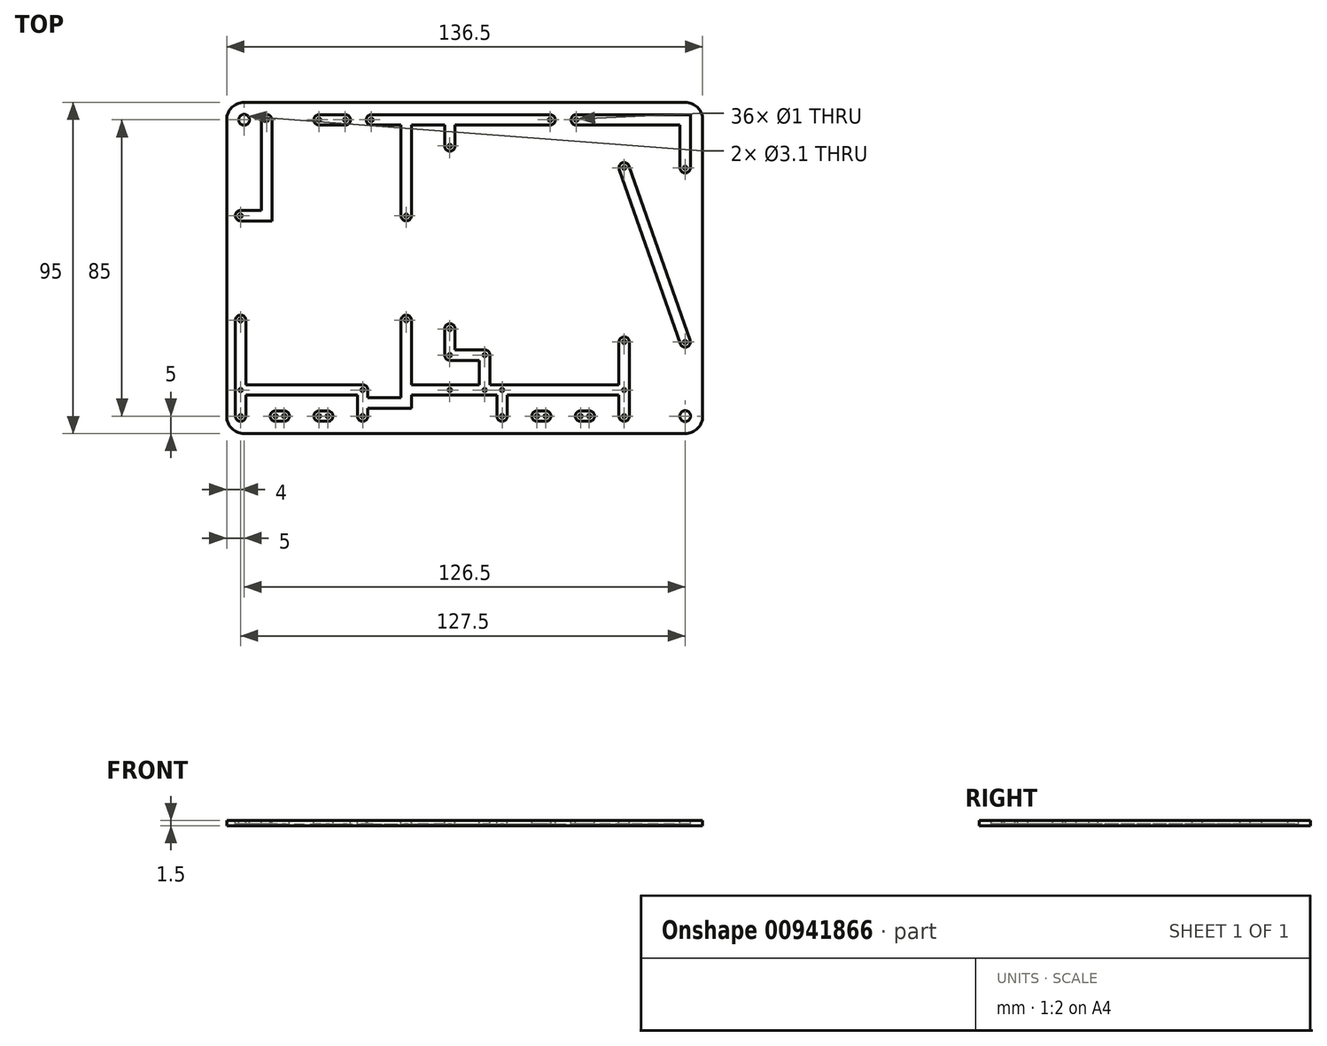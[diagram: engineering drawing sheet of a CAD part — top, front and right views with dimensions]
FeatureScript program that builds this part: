
annotation { "Feature Type Name" : "Feature", "Feature Type Description" : "" }
export const myFeature = defineFeature(function(context is Context, id is Id, definition is map)
    precondition{}
    {
        {
            var Q0;
            Q0=qCreatedBy(makeId("Top.planeOp"),FACE);
            var sketch = newSketch(context, id + "F0", { "sketchPlane" : qUnion([Q0])});
            skLineSegment(sketch, "E0", {"start": v(5, 60) * mm, "end": v(5, 7.5) * mm, "construction": true});
            skLineSegment(sketch, "E1", {"start": v(5, 0) * mm, "end": v(5, -10) * mm, "construction": true});
            skLineSegment(sketch, "E2", {"start": v(33.75, 67.5) * mm, "end": v(41.25, 67.5) * mm, "construction": true});
            skPoint(sketch, "E3", {"position": v(33.75, 67.5) * mm});
            skPoint(sketch, "E4.orphan", {"position": v(5, 67.5) * mm});
            skLineSegment(sketch, "E5", {"start": v(15, 0) * mm, "end": v(15, -10) * mm, "construction": true});
            skPoint(sketch, "E6", {"position": v(5, -17.5) * mm});
            skLineSegment(sketch, "E7", {"start": v(20, -17.5) * mm, "end": v(55, -17.5) * mm, "construction": true});
            skPoint(sketch, "E8", {"position": v(30, -17.5) * mm});
            skPoint(sketch, "E9", {"position": v(32.5, -17.5) * mm});
            skPoint(sketch, "E10", {"position": v(42.5, -17.5) * mm});
            skPoint(sketch, "E11", {"position": v(45, -17.5) * mm});
            skPoint(sketch, "E12", {"position": v(37.5, 67.5) * mm});
            skPoint(sketch, "E13", {"position": v(37.5, -17.5) * mm});
            skLineSegment(sketch, "E14", {"start": v(-7.5, 40) * mm, "end": v(-7.5, 10) * mm, "construction": true});
            skLineSegment(sketch, "E15", {"start": v(-7.5, 25) * mm, "end": v(0, 25) * mm, "construction": true});
            skPoint(sketch, "E16", {"position": v(-7.5, 40) * mm});
            skPoint(sketch, "E17.MirrorP", {"position": v(-7.5, 10) * mm});
            skPoint(sketch, "E18.orphan", {"position": v(-7.5, 67.5) * mm});
            skPoint(sketch, "E19.orphan", {"position": v(-7.5, -17.5) * mm});
            skLineSegment(sketch, "E20", {"start": v(-17.5, 67.5) * mm, "end": v(-25, 67.5) * mm, "construction": true});
            skLineSegment(sketch, "E21", {"start": v(-32.5, 67.5) * mm, "end": v(-47.5, 67.5) * mm, "construction": true});
            skLineSegment(sketch, "E22", {"start": v(-55, 40) * mm, "end": v(-55, 10) * mm, "construction": true});
            skPoint(sketch, "E23", {"position": v(-55, 40) * mm});
            skPoint(sketch, "E24", {"position": v(-55, 10) * mm});
            skPoint(sketch, "E25.orphan", {"position": v(-55, 67.5) * mm});
            skPoint(sketch, "E26.orphan", {"position": v(-55, -17.5) * mm});
            skPoint(sketch, "E27.MirrorP", {"position": v(-45, -17.5) * mm});
            skLineSegment(sketch, "E28.MirrorCS", {"start": v(-20, -17.5) * mm, "end": v(-55, -17.5) * mm, "construction": true});
            skPoint(sketch, "E29.MirrorP", {"position": v(-30, -17.5) * mm});
            skPoint(sketch, "E30.MirrorP", {"position": v(-37.5, -17.5) * mm});
            skPoint(sketch, "E31.MirrorP", {"position": v(-42.5, -17.5) * mm});
            skPoint(sketch, "E32.MirrorP", {"position": v(-32.5, -17.5) * mm});
            skLineSegment(sketch, "E33", {"start": v(-55, -10) * mm, "end": v(-20, -10) * mm, "construction": true});
            skLineSegment(sketch, "E34.MirrorCS", {"start": v(55, -10) * mm, "end": v(20, -10) * mm, "construction": true});
            skLineSegment(sketch, "E35", {"start": v(55, 53.75) * mm, "end": v(55, 3.75) * mm, "construction": true});
            skPoint(sketch, "E36", {"position": v(55, 28.75) * mm});
            skPoint(sketch, "E37", {"position": v(55, 53.75) * mm});
            skLineSegment(sketch, "E38", {"start": v(55, 28.75) * mm, "end": v(72.5, 28.75) * mm, "construction": true});
            skPoint(sketch, "E39.MirrorP", {"position": v(55, 3.75) * mm});
            skPoint(sketch, "E40.orphan", {"position": v(55, 67.5) * mm});
            skLineSegment(sketch, "E41", {"start": v(63.75, 28.75) * mm, "end": v(63.75, 53.75) * mm, "construction": true});
            skLineSegment(sketch, "E42.MirrorCS", {"start": v(72.5, 53.75) * mm, "end": v(72.5, 3.75) * mm, "construction": true});
            skLineSegment(sketch, "E43.bottom", {"start": v(77.5, -27.5) * mm, "end": v(-77.5, -27.5) * mm});
            skLineSegment(sketch, "E43.top", {"start": v(77.5, 85) * mm, "end": v(-77.5, 85) * mm});
            skLineSegment(sketch, "E43.left", {"start": v(82.5, -22.5) * mm, "end": v(82.5, 80) * mm});
            skLineSegment(sketch, "E43.right", {"start": v(-82.5, -22.5) * mm, "end": v(-82.5, 80) * mm});
            skPoint(sketch, "E43.middle", {"position": v(0, 28.75) * mm});
            skPoint(sketch, "E44.visualSharp", {"position": v(-82.5, 85) * mm});
            skArc(sketch, "E44.filletArc", {"start": v(-77.5, 85) * mm, "mid": v(-81.04, 83.54) * mm, "end": v(-82.5, 80) * mm});
            skPoint(sketch, "E45.visualSharp", {"position": v(82.5, 85) * mm});
            skArc(sketch, "E45.filletArc", {"start": v(82.5, 80) * mm, "mid": v(81.04, 83.54) * mm, "end": v(77.5, 85) * mm});
            skPoint(sketch, "E46.visualSharp", {"position": v(82.5, -27.5) * mm});
            skArc(sketch, "E46.filletArc", {"start": v(77.5, -27.5) * mm, "mid": v(81.04, -26.04) * mm, "end": v(82.5, -22.5) * mm});
            skPoint(sketch, "E47.visualSharp", {"position": v(-82.5, -27.5) * mm});
            skArc(sketch, "E47.filletArc", {"start": v(-82.5, -22.5) * mm, "mid": v(-81.04, -26.04) * mm, "end": v(-77.5, -27.5) * mm});
            skCircle(sketch, "E48", {"center": v(-55, 40) * mm, "radius": 0.5 * mm});
            skCircle(sketch, "E49", {"center": v(-55, 10) * mm, "radius": 0.5 * mm});
            skCircle(sketch, "E50", {"center": v(-7.5, 40) * mm, "radius": 0.5 * mm});
            skCircle(sketch, "E51", {"center": v(-7.5, 10) * mm, "radius": 0.5 * mm});
            skCircle(sketch, "E52", {"center": v(-55, -10) * mm, "radius": 0.5 * mm});
            skCircle(sketch, "E53", {"center": v(-20, -10) * mm, "radius": 0.5 * mm});
            skCircle(sketch, "E54", {"center": v(-55, -17.5) * mm, "radius": 0.5 * mm});
            skCircle(sketch, "E55", {"center": v(-45, -17.5) * mm, "radius": 0.5 * mm});
            skCircle(sketch, "E56", {"center": v(-42.5, -17.5) * mm, "radius": 0.5 * mm});
            skCircle(sketch, "E57", {"center": v(-37.5, -17.5) * mm, "radius": 0.5 * mm, "construction": true});
            skCircle(sketch, "E58", {"center": v(-32.5, -17.5) * mm, "radius": 0.5 * mm});
            skCircle(sketch, "E59", {"center": v(-30, -17.5) * mm, "radius": 0.5 * mm});
            skCircle(sketch, "E60", {"center": v(-20, -17.5) * mm, "radius": 0.5 * mm});
            skCircle(sketch, "E61", {"center": v(-47.5, 67.5) * mm, "radius": 0.5 * mm});
            skCircle(sketch, "E62", {"center": v(-32.5, 67.5) * mm, "radius": 0.5 * mm});
            skCircle(sketch, "E63", {"center": v(-25, 67.5) * mm, "radius": 0.5 * mm});
            skCircle(sketch, "E64", {"center": v(-17.5, 67.5) * mm, "radius": 0.5 * mm});
            skCircle(sketch, "E65", {"center": v(5, 60) * mm, "radius": 0.5 * mm});
            skCircle(sketch, "E66", {"center": v(5, 7.5) * mm, "radius": 0.5 * mm});
            skCircle(sketch, "E67", {"center": v(33.75, 67.5) * mm, "radius": 0.5 * mm});
            skCircle(sketch, "E68", {"center": v(41.25, 67.5) * mm, "radius": 0.5 * mm});
            skCircle(sketch, "E69", {"center": v(55, 53.75) * mm, "radius": 0.5 * mm});
            skCircle(sketch, "E70", {"center": v(72.5, 53.75) * mm, "radius": 0.5 * mm});
            skCircle(sketch, "E71", {"center": v(55, 3.75) * mm, "radius": 0.5 * mm});
            skCircle(sketch, "E72", {"center": v(72.5, 3.75) * mm, "radius": 0.5 * mm});
            skCircle(sketch, "E73", {"center": v(55, -10) * mm, "radius": 0.5 * mm});
            skCircle(sketch, "E74", {"center": v(20, -10) * mm, "radius": 0.5 * mm});
            skCircle(sketch, "E75", {"center": v(15, 0) * mm, "radius": 0.5 * mm});
            skCircle(sketch, "E76", {"center": v(15, -10) * mm, "radius": 0.5 * mm});
            skCircle(sketch, "E77", {"center": v(5, 0) * mm, "radius": 0.5 * mm});
            skCircle(sketch, "E78", {"center": v(5, -10) * mm, "radius": 0.5 * mm});
            skCircle(sketch, "E79", {"center": v(20, -17.5) * mm, "radius": 0.5 * mm});
            skCircle(sketch, "E80", {"center": v(30, -17.5) * mm, "radius": 0.5 * mm});
            skCircle(sketch, "E81", {"center": v(32.5, -17.5) * mm, "radius": 0.5 * mm});
            skCircle(sketch, "E82", {"center": v(37.5, -17.5) * mm, "radius": 0.5 * mm, "construction": true});
            skCircle(sketch, "E83", {"center": v(42.5, -17.5) * mm, "radius": 0.5 * mm});
            skCircle(sketch, "E84", {"center": v(45, -17.5) * mm, "radius": 0.5 * mm});
            skCircle(sketch, "E85", {"center": v(55, -17.5) * mm, "radius": 0.5 * mm});
            skSolve(sketch);
        }
        {
            var Q0;
            Q0 = qSketchRegion(id + "F0", true);
            extrude(context, id + "F1", {"entities" : qUnion([Q0]), "depth" : 1.5 * mm, "offsetDistance" : 25 * mm});
        }
        {
            var Q0;
            Q0=makeQuery(id+"F1.opExtrude","CAP_FACE",FACE,{"disambiguationData":[OSD([sQuery(id+"F0.wireOp",EDGE,"E43.bottom"),sQuery(id+"F0.wireOp",EDGE,"E43.top"),sQuery(id+"F0.wireOp",EDGE,"E43.left"),sQuery(id+"F0.wireOp",EDGE,"E43.right"),sQuery(id+"F0.wireOp",EDGE,"E44.filletArc"),sQuery(id+"F0.wireOp",EDGE,"E45.filletArc"),sQuery(id+"F0.wireOp",EDGE,"E46.filletArc"),sQuery(id+"F0.wireOp",EDGE,"E47.filletArc"),sQuery(id+"F0.wireOp",EDGE,"E48"),sQuery(id+"F0.wireOp",EDGE,"E49"),sQuery(id+"F0.wireOp",EDGE,"E50"),sQuery(id+"F0.wireOp",EDGE,"E51"),sQuery(id+"F0.wireOp",EDGE,"E52"),sQuery(id+"F0.wireOp",EDGE,"E53"),sQuery(id+"F0.wireOp",EDGE,"E54"),sQuery(id+"F0.wireOp",EDGE,"E55"),sQuery(id+"F0.wireOp",EDGE,"E56"),sQuery(id+"F0.wireOp",EDGE,"E58"),sQuery(id+"F0.wireOp",EDGE,"E59"),sQuery(id+"F0.wireOp",EDGE,"E60"),sQuery(id+"F0.wireOp",EDGE,"E61"),sQuery(id+"F0.wireOp",EDGE,"E62"),sQuery(id+"F0.wireOp",EDGE,"E63"),sQuery(id+"F0.wireOp",EDGE,"E64"),sQuery(id+"F0.wireOp",EDGE,"E65"),sQuery(id+"F0.wireOp",EDGE,"E66"),sQuery(id+"F0.wireOp",EDGE,"E67"),sQuery(id+"F0.wireOp",EDGE,"E68"),sQuery(id+"F0.wireOp",EDGE,"E69"),sQuery(id+"F0.wireOp",EDGE,"E70"),sQuery(id+"F0.wireOp",EDGE,"E71"),sQuery(id+"F0.wireOp",EDGE,"E72"),sQuery(id+"F0.wireOp",EDGE,"E73"),sQuery(id+"F0.wireOp",EDGE,"E74"),sQuery(id+"F0.wireOp",EDGE,"E75"),sQuery(id+"F0.wireOp",EDGE,"E76"),sQuery(id+"F0.wireOp",EDGE,"E77"),sQuery(id+"F0.wireOp",EDGE,"E78"),sQuery(id+"F0.wireOp",EDGE,"E79"),sQuery(id+"F0.wireOp",EDGE,"E80"),sQuery(id+"F0.wireOp",EDGE,"E81"),sQuery(id+"F0.wireOp",EDGE,"E83"),sQuery(id+"F0.wireOp",EDGE,"E84"),sQuery(id+"F0.wireOp",EDGE,"E85")])],"isStart":false});
            var sketch = newSketch(context, id + "F2", { "sketchPlane" : qUnion([Q0])});
            skLineSegment(sketch, "E86", {"start": v(6.5, 66) * mm, "end": v(33.75, 66) * mm});
            skLineSegment(sketch, "E87", {"start": v(6.5, 66) * mm, "end": v(6.5, 60) * mm});
            skLineSegment(sketch, "E88", {"start": v(53.5, -8.5) * mm, "end": v(53.5, 3.75) * mm});
            skCircle(sketch, "E89", {"center": v(55, 3.75) * mm, "radius": 1.5 * mm});
            skPoint(sketch, "E90", {"position": v(55, 2.25) * mm});
            skPoint(sketch, "E91", {"position": v(53.5, 3.75) * mm});
            skLineSegment(sketch, "E92", {"start": v(56.5, 3.75) * mm, "end": v(56.5, -17.5) * mm});
            skLineSegment(sketch, "E93", {"start": v(45, -19) * mm, "end": v(42.5, -19) * mm});
            skLineSegment(sketch, "E94", {"start": v(18.5, -17.5) * mm, "end": v(18.5, -11.5) * mm});
            skLineSegment(sketch, "E95", {"start": v(55, -17.5) * mm, "end": v(20, -10) * mm, "construction": true});
            skPoint(sketch, "E96.middle", {"position": v(37.5, -13.75) * mm});
            skCircle(sketch, "E97", {"center": v(20, -17.5) * mm, "radius": 1.5 * mm});
            skArc(sketch, "E98", {"start": v(30, -16) * mm, "mid": v(28.5, -17.5) * mm, "end": v(30, -19) * mm});
            skArc(sketch, "E99", {"start": v(32.5, -19) * mm, "mid": v(34, -17.5) * mm, "end": v(32.5, -16) * mm});
            skCircle(sketch, "E100", {"center": v(20, -10) * mm, "radius": 1.5 * mm});
            skCircle(sketch, "E101", {"center": v(15, -10) * mm, "radius": 1.5 * mm});
            skCircle(sketch, "E102", {"center": v(15, 0) * mm, "radius": 1.5 * mm});
            skCircle(sketch, "E103", {"center": v(5, 0) * mm, "radius": 1.5 * mm});
            skCircle(sketch, "E104", {"center": v(5, -10) * mm, "radius": 1.5 * mm});
            skCircle(sketch, "E105", {"center": v(5, 60) * mm, "radius": 1.5 * mm});
            skCircle(sketch, "E106", {"center": v(5, 7.5) * mm, "radius": 1.5 * mm});
            skLineSegment(sketch, "E107.trimOffspring", {"start": v(6.5, 7.5) * mm, "end": v(6.5, 1.5) * mm});
            skPoint(sketch, "E108", {"position": v(15, -8.5) * mm});
            skLineSegment(sketch, "E109", {"start": v(15, -8.5) * mm, "end": v(53.5, -8.5) * mm});
            skLineSegment(sketch, "E110.MirrorCS", {"start": v(56.5, -16) * mm, "end": v(55, -16) * mm, "construction": true});
            skArc(sketch, "E111", {"start": v(53.53, -17.19) * mm, "mid": v(54.84, -19) * mm, "end": v(56.5, -17.5) * mm});
            skArc(sketch, "E112", {"start": v(42.5, -16) * mm, "mid": v(41, -17.5) * mm, "end": v(42.5, -19) * mm});
            skArc(sketch, "E113", {"start": v(45, -19) * mm, "mid": v(46.5, -17.5) * mm, "end": v(45, -16) * mm});
            skLineSegment(sketch, "E114.trimOffspring", {"start": v(32.5, -19) * mm, "end": v(30, -19) * mm});
            skLineSegment(sketch, "E115.trimOffspring", {"start": v(32.5, -16) * mm, "end": v(30, -16) * mm});
            skLineSegment(sketch, "E116.trimOffspring", {"start": v(45, -16) * mm, "end": v(42.5, -16) * mm});
            skPoint(sketch, "E117.orphan", {"position": v(56.5, -19) * mm});
            skCircle(sketch, "E118", {"center": v(55, -10) * mm, "radius": 1.5 * mm});
            skLineSegment(sketch, "E119.0", {"start": v(55, -10) * mm, "end": v(20, -10) * mm, "construction": true});
            skLineSegment(sketch, "E120", {"start": v(21.5, -10) * mm, "end": v(21.5, -10.32) * mm, "construction": true});
            skLineSegment(sketch, "E121", {"start": v(5, -11.5) * mm, "end": v(18.5, -11.5) * mm});
            skLineSegment(sketch, "E122", {"start": v(53.5, -17.5) * mm, "end": v(53.5, -11.5) * mm});
            skCircle(sketch, "E123", {"center": v(-7.5, 40) * mm, "radius": 1.5 * mm});
            skCircle(sketch, "E124", {"center": v(-7.5, 10) * mm, "radius": 1.5 * mm});
            skLineSegment(sketch, "E125", {"start": v(-9, 40) * mm, "end": v(-9, 66) * mm});
            skLineSegment(sketch, "E126.MirrorCS", {"start": v(-6, 40) * mm, "end": v(-6, 67.5) * mm});
            skLineSegment(sketch, "E127.MirrorCS", {"start": v(-9, 10) * mm, "end": v(-9, -12.25) * mm});
            skLineSegment(sketch, "E128.MirrorCS", {"start": v(-6, 10) * mm, "end": v(-6, -8.5) * mm});
            skLineSegment(sketch, "E129.MirrorCS", {"start": v(55, 60) * mm, "end": v(20, 60) * mm, "construction": true});
            skLineSegment(sketch, "E130", {"start": v(5, -8.5) * mm, "end": v(15, -8.5) * mm});
            skLineSegment(sketch, "E131", {"start": v(5, -1.5) * mm, "end": v(15, -1.5) * mm});
            skLineSegment(sketch, "E132", {"start": v(6.5, 1.5) * mm, "end": v(15, 1.5) * mm});
            skPoint(sketch, "E133.orphan", {"position": v(6.5, 0) * mm});
            skPoint(sketch, "E134.orphan", {"position": v(5, 1.5) * mm});
            skLineSegment(sketch, "E135.MirrorCS", {"start": v(3.5, 7.5) * mm, "end": v(3.5, 1.5) * mm});
            skLineSegment(sketch, "E136", {"start": v(3.5, 0) * mm, "end": v(3.5, 1.5) * mm});
            skLineSegment(sketch, "E137", {"start": v(5, -8.5) * mm, "end": v(-6, -8.5) * mm});
            skLineSegment(sketch, "E138", {"start": v(5, -11.5) * mm, "end": v(-6, -11.5) * mm});
            skCircle(sketch, "E139", {"center": v(-20, -10) * mm, "radius": 1.5 * mm});
            skCircle(sketch, "E140", {"center": v(-20, -17.5) * mm, "radius": 1.5 * mm});
            skLineSegment(sketch, "E141.MirrorCS", {"start": v(-32.5, -16) * mm, "end": v(-30, -16) * mm});
            skLineSegment(sketch, "E142.MirrorCS", {"start": v(-32.5, -19) * mm, "end": v(-30, -19) * mm});
            skLineSegment(sketch, "E143.MirrorCS", {"start": v(-45, -16) * mm, "end": v(-42.5, -16) * mm});
            skLineSegment(sketch, "E144.MirrorCS", {"start": v(-45, -19) * mm, "end": v(-42.5, -19) * mm});
            skArc(sketch, "E145.MirrorCS", {"start": v(-42.5, -16) * mm, "mid": v(-41, -17.5) * mm, "end": v(-42.5, -19) * mm});
            skArc(sketch, "E146.MirrorCS", {"start": v(-45, -19) * mm, "mid": v(-46.5, -17.5) * mm, "end": v(-45, -16) * mm});
            skArc(sketch, "E147.MirrorCS", {"start": v(-32.5, -19) * mm, "mid": v(-34, -17.5) * mm, "end": v(-32.5, -16) * mm});
            skArc(sketch, "E148.MirrorCS", {"start": v(-30, -16) * mm, "mid": v(-28.5, -17.5) * mm, "end": v(-30, -19) * mm});
            skLineSegment(sketch, "E149", {"start": v(-21.5, -11.5) * mm, "end": v(-21.5, -17.5) * mm});
            skLineSegment(sketch, "E150", {"start": v(-18.5, -10) * mm, "end": v(-18.5, -12.25) * mm});
            skLineSegment(sketch, "E151", {"start": v(-18.5, -13.75) * mm, "end": v(-6, -13.75) * mm, "construction": true});
            skLineSegment(sketch, "E152", {"start": v(-18.5, -15.25) * mm, "end": v(-6, -15.25) * mm});
            skLineSegment(sketch, "E153.MirrorCS", {"start": v(-18.5, -12.25) * mm, "end": v(-9, -12.25) * mm});
            skPoint(sketch, "E154.orphan", {"position": v(-9, -17.5) * mm});
            skPoint(sketch, "E155.orphan", {"position": v(-6, -17.5) * mm});
            skCircle(sketch, "E156", {"center": v(-55, -10) * mm, "radius": 1.5 * mm});
            skCircle(sketch, "E157.MirrorC", {"center": v(-55, -17.5) * mm, "radius": 1.5 * mm});
            skLineSegment(sketch, "E158.0", {"start": v(-55, -10) * mm, "end": v(-20, -10) * mm, "construction": true});
            skLineSegment(sketch, "E159", {"start": v(-37.5, -10) * mm, "end": v(-37.5, -17.5) * mm, "construction": true});
            skPoint(sketch, "E160.0", {"position": v(-37.5, -17.5) * mm});
            skLineSegment(sketch, "E161.MirrorCS", {"start": v(-53.5, -11.5) * mm, "end": v(-53.5, -17.5) * mm});
            skLineSegment(sketch, "E162.MirrorCS", {"start": v(-56.5, -10) * mm, "end": v(-56.5, -17.5) * mm});
            skCircle(sketch, "E163", {"center": v(-55, 40) * mm, "radius": 1.5 * mm});
            skCircle(sketch, "E164", {"center": v(-55, 10) * mm, "radius": 1.5 * mm});
            skLineSegment(sketch, "E165.trimOffspring", {"start": v(-18.5, -15.25) * mm, "end": v(-18.5, -17.5) * mm});
            skPoint(sketch, "E166.orphan", {"position": v(-6, -12.25) * mm});
            skLineSegment(sketch, "E167.trimOffspring", {"start": v(-6, -11.5) * mm, "end": v(-6, -15.25) * mm});
            skLineSegment(sketch, "E168.trimOffspring", {"start": v(21.5, -11.5) * mm, "end": v(21.5, -17.5) * mm});
            skLineSegment(sketch, "E169.trimOffspring", {"start": v(21.5, -11.5) * mm, "end": v(53.5, -11.5) * mm});
            skLineSegment(sketch, "E170", {"start": v(-55, 10) * mm, "end": v(-55, 10) * mm});
            skLineSegment(sketch, "E171", {"start": v(-55, 10) * mm, "end": v(-55, -10) * mm, "construction": true});
            skLineSegment(sketch, "E172", {"start": v(-56.5, 8.5) * mm, "end": v(-56.5, -10) * mm});
            skLineSegment(sketch, "E173.MirrorCS", {"start": v(-53.5, 8.5) * mm, "end": v(-53.5, -8.5) * mm});
            skLineSegment(sketch, "E174.MirrorCS", {"start": v(-56.5, 11.5) * mm, "end": v(-55, 11.5) * mm});
            skLineSegment(sketch, "E175", {"start": v(-55, 11.5) * mm, "end": v(-53.5, 11.5) * mm});
            skLineSegment(sketch, "E176", {"start": v(-53.5, 10) * mm, "end": v(-53.5, 8.5) * mm});
            skLineSegment(sketch, "E177", {"start": v(-53.5, -11.5) * mm, "end": v(-21.5, -11.5) * mm});
            skLineSegment(sketch, "E178.MirrorCS", {"start": v(-53.5, -8.5) * mm, "end": v(-21.5, -8.5) * mm});
            skLineSegment(sketch, "E179", {"start": v(-21.5, -8.5) * mm, "end": v(-20, -8.5) * mm});
            skPoint(sketch, "E180.orphan", {"position": v(-53.5, -10) * mm});
            skPoint(sketch, "E181.orphan", {"position": v(-21.5, -10) * mm});
            skLineSegment(sketch, "E182.MirrorCS", {"start": v(-56.5, 38.5) * mm, "end": v(-55, 38.5) * mm});
            skLineSegment(sketch, "E183.MirrorCS", {"start": v(-56.5, 41.5) * mm, "end": v(-55, 41.5) * mm});
            skCircle(sketch, "E184", {"center": v(-47.5, 67.5) * mm, "radius": 1.5 * mm});
            skLineSegment(sketch, "E185", {"start": v(-49, 67.5) * mm, "end": v(-49, 41.5) * mm});
            skLineSegment(sketch, "E186", {"start": v(-49, 41.5) * mm, "end": v(-56.5, 41.5) * mm});
            skLineSegment(sketch, "E187", {"start": v(-46, 67.5) * mm, "end": v(-46, 38.5) * mm});
            skLineSegment(sketch, "E188", {"start": v(-46, 38.5) * mm, "end": v(-56.5, 38.5) * mm});
            skCircle(sketch, "E189", {"center": v(-32.5, 67.5) * mm, "radius": 1.5 * mm});
            skCircle(sketch, "E190", {"center": v(-25, 67.5) * mm, "radius": 1.5 * mm});
            skCircle(sketch, "E191", {"center": v(-17.5, 67.5) * mm, "radius": 1.5 * mm});
            skLineSegment(sketch, "E192", {"start": v(-32.5, 69) * mm, "end": v(-25, 69) * mm});
            skLineSegment(sketch, "E193", {"start": v(-17.5, 69) * mm, "end": v(-6, 69) * mm});
            skLineSegment(sketch, "E194", {"start": v(-6, 69) * mm, "end": v(-6, 67.5) * mm});
            skLineSegment(sketch, "E195.MirrorCS", {"start": v(-32.5, 66) * mm, "end": v(-25, 66) * mm});
            skLineSegment(sketch, "E196.MirrorCS", {"start": v(-17.5, 66) * mm, "end": v(-9, 66) * mm});
            skPoint(sketch, "E197.orphan", {"position": v(-9, 67.5) * mm});
            skPoint(sketch, "E198.orphan", {"position": v(-6, 66) * mm});
            skLineSegment(sketch, "E199.MirrorCS", {"start": v(3.5, 66) * mm, "end": v(3.5, 60) * mm});
            skCircle(sketch, "E200", {"center": v(33.75, 67.5) * mm, "radius": 1.5 * mm});
            skCircle(sketch, "E201", {"center": v(41.25, 67.5) * mm, "radius": 1.5 * mm});
            skLineSegment(sketch, "E202.trimOffspring", {"start": v(41.25, 66) * mm, "end": v(53.5, 66) * mm});
            skLineSegment(sketch, "E203", {"start": v(3.5, 66) * mm, "end": v(-6, 66) * mm});
            skLineSegment(sketch, "E204", {"start": v(-6, 69) * mm, "end": v(33.75, 69) * mm});
            skLineSegment(sketch, "E205", {"start": v(13.5, -1.5) * mm, "end": v(13.5, -8.5) * mm});
            skLineSegment(sketch, "E206.MirrorCS", {"start": v(16.5, -1.5) * mm, "end": v(16.5, -8.5) * mm});
            skLineSegment(sketch, "E207", {"start": v(16.5, -1.5) * mm, "end": v(16.5, 0) * mm});
            skCircle(sketch, "E208", {"center": v(72.5, 3.75) * mm, "radius": 1.5 * mm});
            skCircle(sketch, "E209", {"center": v(55, 53.75) * mm, "radius": 1.5 * mm});
            skCircle(sketch, "E210", {"center": v(72.5, 53.75) * mm, "radius": 1.5 * mm});
            skLineSegment(sketch, "E211", {"start": v(55, 53.75) * mm, "end": v(72.5, 3.75) * mm, "construction": true});
            skLineSegment(sketch, "E212", {"start": v(53.58, 53.25) * mm, "end": v(71.08, 3.25) * mm});
            skLineSegment(sketch, "E213.MirrorCS", {"start": v(56.42, 54.25) * mm, "end": v(73.92, 4.25) * mm});
            skLineSegment(sketch, "E214", {"start": v(71, 53.75) * mm, "end": v(71, 66) * mm});
            skLineSegment(sketch, "E215", {"start": v(71, 66) * mm, "end": v(53.5, 66) * mm});
            skLineSegment(sketch, "E216", {"start": v(41.25, 69) * mm, "end": v(71, 69) * mm});
            skLineSegment(sketch, "E217", {"start": v(74, 53.75) * mm, "end": v(74, 69) * mm});
            skLineSegment(sketch, "E218", {"start": v(74, 69) * mm, "end": v(71, 69) * mm});
            skLineSegment(sketch, "E219.MirrorCS", {"start": v(-56.5, 10) * mm, "end": v(-56.5, 8.5) * mm});
            skPoint(sketch, "E220.orphan", {"position": v(-56.5, 11.5) * mm});
            skPoint(sketch, "E221.start.orphan", {"position": v(-55, 8.5) * mm});
            skSolve(sketch);
        }
        {
            var Q0;
            Q0 = qSketchRegion(id + "F2", true);
            extrude(context, id + "F3", {"entities" : qUnion([Q0]), "operationType" : NewBodyOperationType.REMOVE, "oppositeDirection" : true, "depth" : 1 * mm, "offsetDistance" : 25 * mm});
        }
        {
            var Q0;
            Q0=makeQuery(id+"F1.opExtrude","CAP_FACE",FACE,{"disambiguationData":[OSD([sQuery(id+"F0.wireOp",EDGE,"E43.bottom"),sQuery(id+"F0.wireOp",EDGE,"E43.top"),sQuery(id+"F0.wireOp",EDGE,"E43.left"),sQuery(id+"F0.wireOp",EDGE,"E43.right"),sQuery(id+"F0.wireOp",EDGE,"E44.filletArc"),sQuery(id+"F0.wireOp",EDGE,"E45.filletArc"),sQuery(id+"F0.wireOp",EDGE,"E46.filletArc"),sQuery(id+"F0.wireOp",EDGE,"E47.filletArc"),sQuery(id+"F0.wireOp",EDGE,"E48"),sQuery(id+"F0.wireOp",EDGE,"E49"),sQuery(id+"F0.wireOp",EDGE,"E50"),sQuery(id+"F0.wireOp",EDGE,"E51"),sQuery(id+"F0.wireOp",EDGE,"E52"),sQuery(id+"F0.wireOp",EDGE,"E53"),sQuery(id+"F0.wireOp",EDGE,"E54"),sQuery(id+"F0.wireOp",EDGE,"E55"),sQuery(id+"F0.wireOp",EDGE,"E56"),sQuery(id+"F0.wireOp",EDGE,"E58"),sQuery(id+"F0.wireOp",EDGE,"E59"),sQuery(id+"F0.wireOp",EDGE,"E60"),sQuery(id+"F0.wireOp",EDGE,"E61"),sQuery(id+"F0.wireOp",EDGE,"E62"),sQuery(id+"F0.wireOp",EDGE,"E63"),sQuery(id+"F0.wireOp",EDGE,"E64"),sQuery(id+"F0.wireOp",EDGE,"E65"),sQuery(id+"F0.wireOp",EDGE,"E66"),sQuery(id+"F0.wireOp",EDGE,"E67"),sQuery(id+"F0.wireOp",EDGE,"E68"),sQuery(id+"F0.wireOp",EDGE,"E69"),sQuery(id+"F0.wireOp",EDGE,"E70"),sQuery(id+"F0.wireOp",EDGE,"E71"),sQuery(id+"F0.wireOp",EDGE,"E72"),sQuery(id+"F0.wireOp",EDGE,"E73"),sQuery(id+"F0.wireOp",EDGE,"E74"),sQuery(id+"F0.wireOp",EDGE,"E75"),sQuery(id+"F0.wireOp",EDGE,"E76"),sQuery(id+"F0.wireOp",EDGE,"E77"),sQuery(id+"F0.wireOp",EDGE,"E78"),sQuery(id+"F0.wireOp",EDGE,"E79"),sQuery(id+"F0.wireOp",EDGE,"E80"),sQuery(id+"F0.wireOp",EDGE,"E81"),sQuery(id+"F0.wireOp",EDGE,"E83"),sQuery(id+"F0.wireOp",EDGE,"E84"),sQuery(id+"F0.wireOp",EDGE,"E85")])],"isStart":false});
            var sketch = newSketch(context, id + "F4", { "sketchPlane" : qUnion([Q0])});
            skCircle(sketch, "E222.0", {"center": v(-17.5, 67.5) * mm, "radius": 0.5 * mm, "construction": true});
            skLineSegment(sketch, "E223", {"start": v(0, 67.5) * mm, "end": v(0, -17.5) * mm, "construction": true});
            skLineSegment(sketch, "E224.bottom", {"start": v(-54, 72.5) * mm, "end": v(72.5, 72.5) * mm});
            skLineSegment(sketch, "E224.top", {"start": v(-54, -22.5) * mm, "end": v(72.5, -22.5) * mm});
            skLineSegment(sketch, "E224.left", {"start": v(-59, 67.5) * mm, "end": v(-59, -17.5) * mm});
            skLineSegment(sketch, "E224.right", {"start": v(77.5, 67.5) * mm, "end": v(77.5, -17.5) * mm});
            skPoint(sketch, "E225.visualSharp", {"position": v(77.5, -22.5) * mm});
            skArc(sketch, "E225.filletArc", {"start": v(72.5, -22.5) * mm, "mid": v(76.04, -21.04) * mm, "end": v(77.5, -17.5) * mm});
            skPoint(sketch, "E226.visualSharp", {"position": v(77.5, 72.5) * mm});
            skArc(sketch, "E226.filletArc", {"start": v(77.5, 67.5) * mm, "mid": v(76.04, 71.04) * mm, "end": v(72.5, 72.5) * mm});
            skPoint(sketch, "E227.visualSharp", {"position": v(-59, 72.5) * mm});
            skArc(sketch, "E227.filletArc", {"start": v(-54, 72.5) * mm, "mid": v(-57.54, 71.04) * mm, "end": v(-59, 67.5) * mm});
            skPoint(sketch, "E228.visualSharp", {"position": v(-59, -22.5) * mm});
            skArc(sketch, "E228.filletArc", {"start": v(-59, -17.5) * mm, "mid": v(-57.54, -21.04) * mm, "end": v(-54, -22.5) * mm});
            skCircle(sketch, "E229", {"center": v(-54, 67.5) * mm, "radius": 1.55 * mm});
            skCircle(sketch, "E230", {"center": v(72.5, 67.5) * mm, "radius": 1.55 * mm, "construction": true});
            skCircle(sketch, "E231", {"center": v(72.5, -17.5) * mm, "radius": 1.55 * mm});
            skCircle(sketch, "E232", {"center": v(-54, -17.5) * mm, "radius": 1.55 * mm, "construction": true});
            skSolve(sketch);
        }
        {
            var Q0;
            Q0=makeQuery(id+"F4.imprint","IMPRINT",FACE,{"disambiguationData":[TD([[makeQuery(id+"F4.imprint","IMPRINT",EDGE,{"derivedFrom":sQuery(id+"F4.wireOp",EDGE,"E224.bottom")}),1.0]])]});
            var Q1;
            Q1=makeQuery(id+"F4.imprint","IMPRINT",FACE,{"disambiguationData":[TD([[makeQuery(id+"F4.imprint","IMPRINT",EDGE,{"derivedFrom":sQuery(id+"F4.wireOp",EDGE,"E229")}),1.0]])]});
            var Q2;
            Q2=makeQuery(id+"F4.imprint","IMPRINT",FACE,{"disambiguationData":[TD([[makeQuery(id+"F4.imprint","IMPRINT",EDGE,{"derivedFrom":sQuery(id+"F4.wireOp",EDGE,"E231")}),1.0]])]});
            extrude(context, id + "F5", {"entities" : qUnion([Q0, Q1, Q2]), "operationType" : NewBodyOperationType.REMOVE, "endBound" : BoundingType.THROUGH_ALL, "oppositeDirection" : true, "depth" : 25 * mm, "offsetDistance" : 25 * mm});
        }
    });
